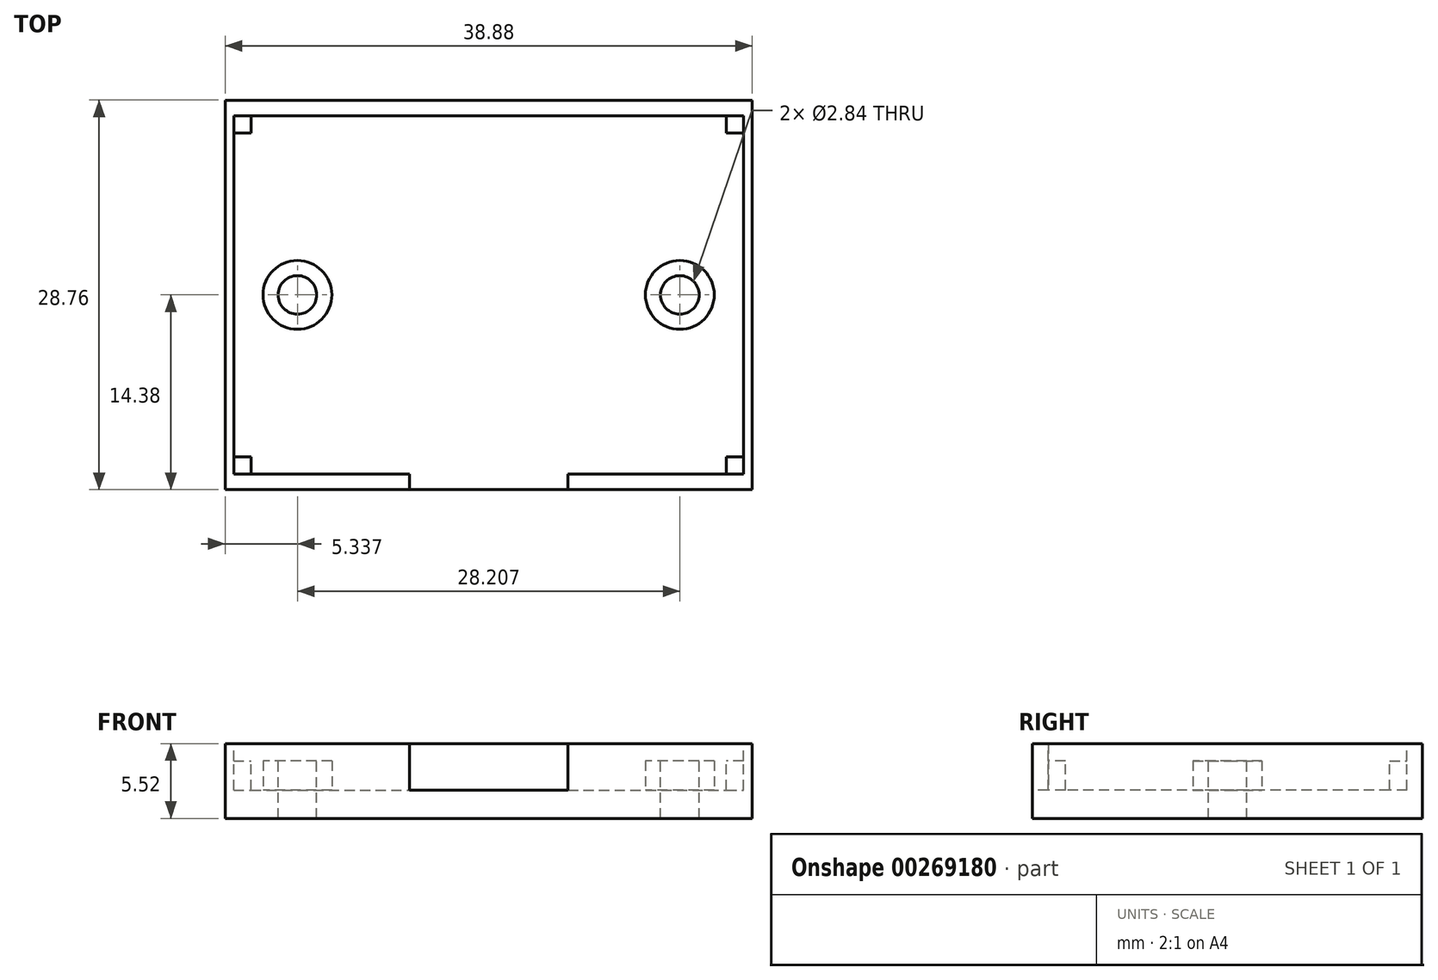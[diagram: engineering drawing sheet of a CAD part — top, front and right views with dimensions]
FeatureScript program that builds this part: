
annotation { "Feature Type Name" : "Feature", "Feature Type Description" : "" }
export const myFeature = defineFeature(function(context is Context, id is Id, definition is map)
    precondition{}
    {
        {
            var Q0;
            Q0=qCreatedBy(makeId("Top.planeOp"),FACE);
            var sketch = newSketch(context, id + "F0", { "sketchPlane" : qUnion([Q0])});
            skLineSegment(sketch, "E0.bottom", {"start": v(19.44, -14.38) * mm, "end": v(-19.44, -14.38) * mm});
            skLineSegment(sketch, "E0.top", {"start": v(19.44, 14.38) * mm, "end": v(-19.44, 14.38) * mm});
            skLineSegment(sketch, "E0.left", {"start": v(19.44, -14.38) * mm, "end": v(19.44, 14.38) * mm});
            skLineSegment(sketch, "E0.right", {"start": v(-19.44, -14.38) * mm, "end": v(-19.44, 14.38) * mm});
            skPoint(sketch, "E0.middle", {"position": v(0, 0) * mm});
            skSolve(sketch);
        }
        {
            var Q0;
            Q0=makeQuery(id+"F0.imprint","IMPRINT",FACE,{"disambiguationData":[TD([[makeQuery(id+"F0.imprint","IMPRINT",EDGE,{"derivedFrom":sQuery(id+"F0.wireOp",EDGE,"E0.bottom")}),-1.0]])]});
            extrude(context, id + "F1", {"entities" : qUnion([Q0]), "depth" : 5.52 * mm});
        }
        {
            var Q0;
            Q0=makeQuery(id+"F1.opExtrude","CAP_FACE",FACE,{"disambiguationData":[OSD([sQuery(id+"F0.wireOp",EDGE,"E0.bottom"),sQuery(id+"F0.wireOp",EDGE,"E0.top"),sQuery(id+"F0.wireOp",EDGE,"E0.left"),sQuery(id+"F0.wireOp",EDGE,"E0.right")])],"isStart":false});
            var sketch = newSketch(context, id + "F2", { "sketchPlane" : qUnion([Q0])});
            skLineSegment(sketch, "E1.bottom", {"start": v(-18.8, 13.23) * mm, "end": v(18.8, 13.23) * mm});
            skLineSegment(sketch, "E1.top", {"start": v(-18.8, -13.23) * mm, "end": v(18.8, -13.23) * mm});
            skLineSegment(sketch, "E1.left", {"start": v(-18.8, 13.23) * mm, "end": v(-18.8, -13.23) * mm});
            skLineSegment(sketch, "E1.right", {"start": v(18.8, 13.23) * mm, "end": v(18.8, -13.23) * mm});
            skPoint(sketch, "E1.middle", {"position": v(0, 0) * mm});
            skSolve(sketch);
        }
        {
            var Q0;
            Q0 = qSketchRegion(id + "F2", true);
            extrude(context, id + "F3", {"entities" : qUnion([Q0]), "operationType" : NewBodyOperationType.REMOVE, "oppositeDirection" : true, "depth" : 3.43 * mm});
        }
        {
            var Q0;
            Q0=makeQuery(id+"F3.boolean.opBoolean","COPY",FACE,{"derivedFrom":makeQuery(id+"F3.opExtrude","SWEPT_FACE",FACE,{"disambiguationData":[OSD([sQuery(id+"F2.wireOp",EDGE,"E1.bottom")])]})});
            var sketch = newSketch(context, id + "F4", { "sketchPlane" : qUnion([Q0])});
            skLineSegment(sketch, "E2.bottom", {"start": v(-18.8, 2.1) * mm, "end": v(-17.53, 2.1) * mm});
            skLineSegment(sketch, "E2.top", {"start": v(-18.8, 4.25) * mm, "end": v(-17.53, 4.25) * mm});
            skLineSegment(sketch, "E2.left", {"start": v(-18.8, 2.1) * mm, "end": v(-18.8, 4.25) * mm});
            skLineSegment(sketch, "E2.right", {"start": v(-17.53, 2.1) * mm, "end": v(-17.53, 4.25) * mm});
            skSolve(sketch);
        }
        {
            var Q0;
            Q0 = qSketchRegion(id + "F4", true);
            extrude(context, id + "F5", {"entities" : qUnion([Q0]), "operationType" : NewBodyOperationType.ADD, "depth" : 1.27 * mm});
        }
        {
            var Q0;
            Q0=makeQuery(id+"F3.boolean.opBoolean","COPY",FACE,{"derivedFrom":makeQuery(id+"F3.opExtrude","SWEPT_FACE",FACE,{"disambiguationData":[OSD([sQuery(id+"F2.wireOp",EDGE,"E1.right")])]})});
            var sketch = newSketch(context, id + "F6", { "sketchPlane" : qUnion([Q0])});
            skLineSegment(sketch, "E3.bottom", {"start": v(-13.23, 2.1) * mm, "end": v(-11.96, 2.1) * mm});
            skLineSegment(sketch, "E3.top", {"start": v(-13.23, 4.25) * mm, "end": v(-11.96, 4.25) * mm});
            skLineSegment(sketch, "E3.left", {"start": v(-13.23, 2.1) * mm, "end": v(-13.23, 4.25) * mm});
            skLineSegment(sketch, "E3.right", {"start": v(-11.96, 2.1) * mm, "end": v(-11.96, 4.25) * mm});
            skSolve(sketch);
        }
        {
            var Q0;
            Q0 = qSketchRegion(id + "F6", true);
            extrude(context, id + "F7", {"entities" : qUnion([Q0]), "operationType" : NewBodyOperationType.ADD, "depth" : 1.27 * mm});
        }
        {
            var Q0;
            Q0=makeQuery(id+"F3.boolean.opBoolean","COPY",FACE,{"derivedFrom":makeQuery(id+"F3.opExtrude","SWEPT_FACE",FACE,{"disambiguationData":[OSD([sQuery(id+"F2.wireOp",EDGE,"E1.top")])]})});
            var sketch = newSketch(context, id + "F8", { "sketchPlane" : qUnion([Q0])});
            skLineSegment(sketch, "E4.bottom", {"start": v(-18.8, 2.1) * mm, "end": v(-17.53, 2.1) * mm});
            skLineSegment(sketch, "E4.top", {"start": v(-18.8, 4.25) * mm, "end": v(-17.53, 4.25) * mm});
            skLineSegment(sketch, "E4.left", {"start": v(-18.8, 2.1) * mm, "end": v(-18.8, 4.25) * mm});
            skLineSegment(sketch, "E4.right", {"start": v(-17.53, 2.1) * mm, "end": v(-17.53, 4.25) * mm});
            skSolve(sketch);
        }
        {
            var Q0;
            Q0 = qSketchRegion(id + "F8", true);
            extrude(context, id + "F9", {"entities" : qUnion([Q0]), "operationType" : NewBodyOperationType.ADD, "depth" : 1.27 * mm});
        }
        {
            var Q0;
            Q0=makeQuery(id+"F3.boolean.opBoolean","COPY",FACE,{"derivedFrom":makeQuery(id+"F3.opExtrude","SWEPT_FACE",FACE,{"disambiguationData":[OSD([sQuery(id+"F2.wireOp",EDGE,"E1.top")])]})});
            var sketch = newSketch(context, id + "F10", { "sketchPlane" : qUnion([Q0])});
            skLineSegment(sketch, "E5.bottom", {"start": v(18.8, 2.1) * mm, "end": v(17.53, 2.1) * mm});
            skLineSegment(sketch, "E5.top", {"start": v(18.8, 4.25) * mm, "end": v(17.53, 4.25) * mm});
            skLineSegment(sketch, "E5.left", {"start": v(18.8, 2.1) * mm, "end": v(18.8, 4.25) * mm});
            skLineSegment(sketch, "E5.right", {"start": v(17.53, 2.1) * mm, "end": v(17.53, 4.25) * mm});
            skSolve(sketch);
        }
        {
            var Q0;
            Q0 = qSketchRegion(id + "F10", true);
            extrude(context, id + "F11", {"entities" : qUnion([Q0]), "operationType" : NewBodyOperationType.ADD, "depth" : 1.27 * mm});
        }
        {
            var Q0;
            Q0=makeQuery(id+"F3.boolean.opBoolean","COPY",FACE,{"derivedFrom":makeQuery(id+"F3.opExtrude","CAP_FACE",FACE,{"disambiguationData":[OSD([sQuery(id+"F2.wireOp",EDGE,"E1.bottom"),sQuery(id+"F2.wireOp",EDGE,"E1.top"),sQuery(id+"F2.wireOp",EDGE,"E1.left"),sQuery(id+"F2.wireOp",EDGE,"E1.right")])],"isStart":false})});
            var sketch = newSketch(context, id + "F12", { "sketchPlane" : qUnion([Q0])});
            skCircle(sketch, "E6", {"center": v(-14.1, 0) * mm, "radius": 2.54 * mm});
            skSolve(sketch);
        }
        {
            var Q0;
            Q0=makeQuery(id+"F12.imprint","IMPRINT",FACE,{"disambiguationData":[TD([[makeQuery(id+"F12.imprint","IMPRINT",EDGE,{"derivedFrom":sQuery(id+"F12.wireOp",EDGE,"E6")}),1.0]])]});
            extrude(context, id + "F13", {"entities" : qUnion([Q0]), "operationType" : NewBodyOperationType.ADD, "depth" : 2.16 * mm});
        }
        {
            var Q0;
            Q0=makeQuery(id+"F13.opExtrude","CAP_FACE",FACE,{"disambiguationData":[OSD([sQuery(id+"F12.wireOp",EDGE,"E6")])],"isStart":false});
            var sketch = newSketch(context, id + "F14", { "sketchPlane" : qUnion([Q0])});
            skCircle(sketch, "E7", {"center": v(-14.1, 0) * mm, "radius": 1.42 * mm});
            skSolve(sketch);
        }
        {
            var Q0;
            Q0 = qSketchRegion(id + "F14", true);
            extrude(context, id + "F15", {"entities" : qUnion([Q0]), "operationType" : NewBodyOperationType.REMOVE, "endBound" : BoundingType.THROUGH_ALL, "oppositeDirection" : true, "depth" : 25.4 * mm});
        }
        {
            var Q0;
            Q0=makeQuery(id+"F3.boolean.opBoolean","COPY",FACE,{"derivedFrom":makeQuery(id+"F3.opExtrude","CAP_FACE",FACE,{"disambiguationData":[OSD([sQuery(id+"F2.wireOp",EDGE,"E1.bottom"),sQuery(id+"F2.wireOp",EDGE,"E1.top"),sQuery(id+"F2.wireOp",EDGE,"E1.left"),sQuery(id+"F2.wireOp",EDGE,"E1.right")])],"isStart":false})});
            var sketch = newSketch(context, id + "F16", { "sketchPlane" : qUnion([Q0])});
            skCircle(sketch, "E8", {"center": v(14.1, 0) * mm, "radius": 2.54 * mm});
            skSolve(sketch);
        }
        {
            var Q0;
            Q0 = qSketchRegion(id + "F16", true);
            extrude(context, id + "F17", {"entities" : qUnion([Q0]), "operationType" : NewBodyOperationType.ADD, "depth" : 2.16 * mm});
        }
        {
            var Q0;
            Q0=makeQuery(id+"F17.opExtrude","CAP_FACE",FACE,{"disambiguationData":[OSD([sQuery(id+"F16.wireOp",EDGE,"E8")])],"isStart":false});
            var sketch = newSketch(context, id + "F18", { "sketchPlane" : qUnion([Q0])});
            skCircle(sketch, "E9", {"center": v(14.1, 0) * mm, "radius": 1.42 * mm});
            skSolve(sketch);
        }
        {
            var Q0;
            Q0 = qSketchRegion(id + "F18", true);
            extrude(context, id + "F19", {"entities" : qUnion([Q0]), "operationType" : NewBodyOperationType.REMOVE, "endBound" : BoundingType.THROUGH_ALL, "oppositeDirection" : true, "depth" : 25.4 * mm});
        }
        {
            var Q0;
            Q0=makeQuery(id+"F1.opExtrude","SWEPT_FACE",FACE,{"disambiguationData":[OSD([sQuery(id+"F0.wireOp",EDGE,"E0.bottom")])]});
            var sketch = newSketch(context, id + "F20", { "sketchPlane" : qUnion([Q0])});
            skLineSegment(sketch, "E10.bottom", {"start": v(-5.85, 5.52) * mm, "end": v(5.85, 5.52) * mm});
            skLineSegment(sketch, "E10.top", {"start": v(-5.85, 2.1) * mm, "end": v(5.85, 2.1) * mm});
            skLineSegment(sketch, "E10.left", {"start": v(-5.85, 5.52) * mm, "end": v(-5.85, 2.1) * mm});
            skLineSegment(sketch, "E10.right", {"start": v(5.85, 5.52) * mm, "end": v(5.85, 2.1) * mm});
            skSolve(sketch);
        }
        {
            var Q0;
            Q0 = qSketchRegion(id + "F20", true);
            extrude(context, id + "F21", {"entities" : qUnion([Q0]), "operationType" : NewBodyOperationType.REMOVE, "oppositeDirection" : true, "depth" : 2.03 * mm});
        }
    });
